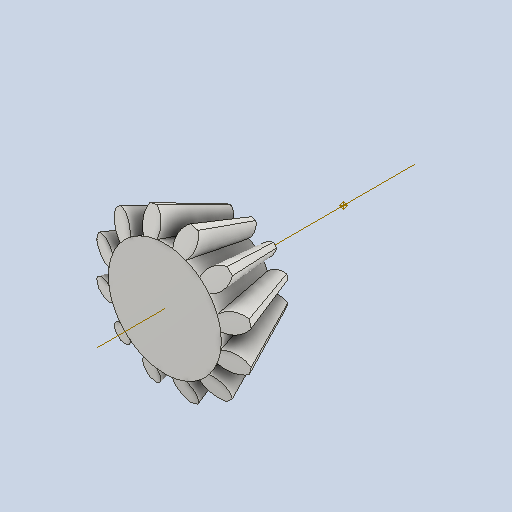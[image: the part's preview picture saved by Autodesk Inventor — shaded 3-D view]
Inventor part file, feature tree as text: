
AUTODESK INVENTOR PART (.ipt)
format: ipt  version: 2022 (Build 260153000, 153)  size: 452,608 bytes
history: native  units: in
note: dims shown in document units (in); Inventor stores cm internally (conversion verified against a paired STEP export)
features: other x30, sketch x1
ambient origin geometry x8: Origin, YZ Plane, XZ Plane, XY Plane, X Axis, Y Axis, Z Axis, Center Point
bodies: Solid1 (feature_tree)
feature tree (31):
  other  "Bevel Gear1"
  other  "Solid1::Bevel Gear1"
  other  "TaggingFeature1"
  other  "Teeth Body Sketch"
  other  "Start Sketch"
  other  "End Sketch"
  other  "End Sketch Right"
  other  "End Sketch Left"
  other  "Body Sketch"
  sketch  "Sketch6"  dims[d0=0.3937in d48=0.0in d49=0.0in d50=90.0deg d52=0.0in d53=0.0in d54=0.0in]
  other  "3D Sketch Right"
  other  "3D Sketch Left"
  other  "Mesh Plane"
  other  "Top Plane"
  other  "Mesh Plane2"
  other  "Tooth Plane"
  other  "End Plane"
  other  "End Plane Right"
  other  "End Plane Left"
  other  "Z Axis_1"
  other  "Top Point"
  other  "Start Point"
  other  "End Point"
  other  "Srf1"
  other  "Srf1::Derived"
  other  "Start plane iMate"
  other  "Mesh iMate2"
  other  "Axis Angle iMate"
  other  "Axis iMate"
  other  "Mesh iMate"
  other  "Intersection iMate"
